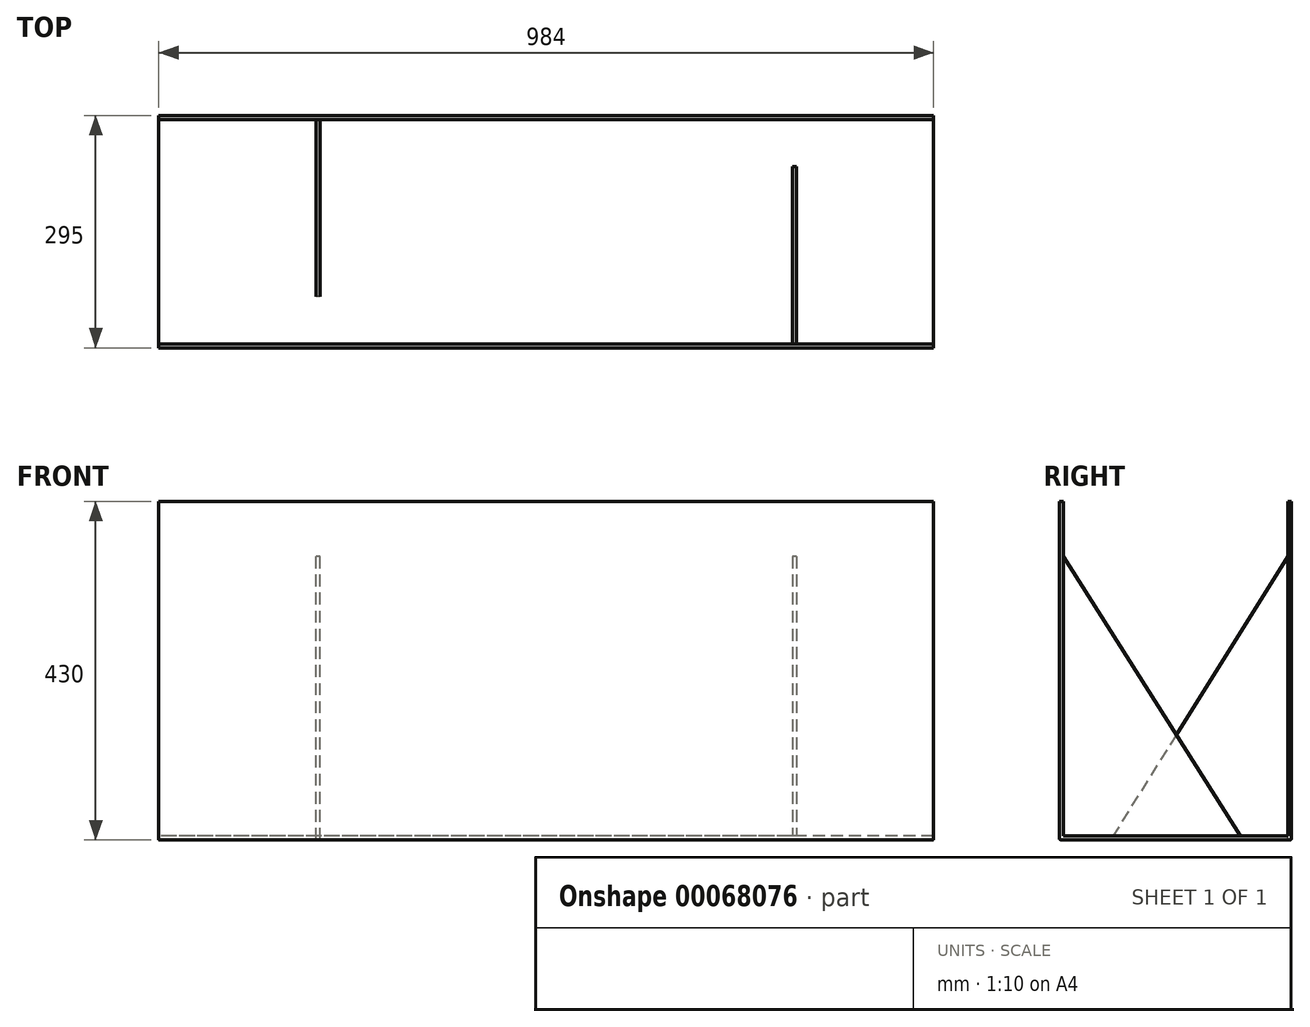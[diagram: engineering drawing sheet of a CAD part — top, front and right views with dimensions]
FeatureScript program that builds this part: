
annotation { "Feature Type Name" : "Feature", "Feature Type Description" : "" }
export const myFeature = defineFeature(function(context is Context, id is Id, definition is map)
    precondition{}
    {
        {
            var Q0;
            Q0=qCreatedBy(makeId("Right.planeOp"),FACE);
            var sketch = newSketch(context, id + "F0", { "sketchPlane" : qUnion([Q0])});
            skLineSegment(sketch, "E0.left", {"start": v(0, 0) * mm, "end": v(0, 430) * mm});
            skLineSegment(sketch, "E1", {"start": v(0, 0) * mm, "end": v(-295, 0) * mm});
            skLineSegment(sketch, "E2", {"start": v(-295, 0) * mm, "end": v(-295, 430) * mm});
            skLineSegment(sketch, "E3.0", {"start": v(-290, 5) * mm, "end": v(-290, 430) * mm});
            skLineSegment(sketch, "E3.1", {"start": v(-5, 5) * mm, "end": v(-290, 5) * mm});
            skLineSegment(sketch, "E3.2", {"start": v(-5, 5) * mm, "end": v(-5, 430) * mm});
            skLineSegment(sketch, "E4", {"start": v(0, 430) * mm, "end": v(-5, 430) * mm});
            skLineSegment(sketch, "E5", {"start": v(-290, 430) * mm, "end": v(-295, 430) * mm});
            skSolve(sketch);
        }
        {
            var Q0;
            Q0=makeQuery(id+"F0.imprint","IMPRINT",FACE,{"disambiguationData":[TD([[makeQuery(id+"F0.imprint","IMPRINT",EDGE,{"derivedFrom":sQuery(id+"F0.wireOp",EDGE,"E0.bottom")}),-1.0]])]});
            var Q1;
            Q1=makeQuery(id+"F0.imprint","IMPRINT",FACE,{"disambiguationData":[TD([[makeQuery(id+"F0.imprint","IMPRINT",EDGE,{"derivedFrom":sQuery(id+"F0.wireOp",EDGE,"E0.left")}),1.0]])]});
            extrude(context, id + "F1", {"entities" : qUnion([Q0, Q1]), "depth" : 984 * mm});
        }
        {
            var Q0;
            Q0=qCreatedBy(makeId("Right.planeOp"),FACE);
            cPlane(context, id + "F2", {"entities" : qUnion([Q0]), "cplaneType" : CPlaneType.OFFSET, "offset" : 200 * mm, "width" : 150 * mm, "height" : 150 * mm});
        }
        {
            var Q0;
            Q0=qCreatedBy(id+"F2.planeOp",FACE);
            var sketch = newSketch(context, id + "F3", { "sketchPlane" : qUnion([Q0])});
            skLineSegment(sketch, "E6.0", {"start": v(-5, 0) * mm, "end": v(-5, 360) * mm});
            skLineSegment(sketch, "E7.0", {"start": v(-5, 0) * mm, "end": v(-230, 0) * mm});
            skPoint(sketch, "E8", {"position": v(-230, 0) * mm});
            skPoint(sketch, "E9", {"position": v(-5, 360) * mm});
            skLineSegment(sketch, "E10", {"start": v(-5, 360) * mm, "end": v(-230, 0) * mm});
            skSolve(sketch);
        }
        {
            var Q0;
            Q0=makeQuery(id+"F3.imprint","IMPRINT",FACE,{"disambiguationData":[TD([[makeQuery(id+"F3.imprint","IMPRINT",EDGE,{"derivedFrom":sQuery(id+"F3.wireOp",EDGE,"E6.0")}),1.0]])]});
            extrude(context, id + "F4", {"entities" : qUnion([Q0]), "depth" : 5 * mm});
        }
        {
            var Q0;
            Q0=makeQuery(id+"F4.opExtrude","CAP_FACE",FACE,{"disambiguationData":[OSD([sQuery(id+"F3.wireOp",EDGE,"E6.0"),sQuery(id+"F3.wireOp",EDGE,"E7.0"),sQuery(id+"F3.wireOp",EDGE,"E10")])],"isStart":false});
            cPlane(context, id + "F5", {"entities" : qUnion([Q0]), "cplaneType" : CPlaneType.OFFSET, "offset" : 600 * mm, "width" : 150 * mm, "height" : 150 * mm});
        }
        {
            var Q0;
            Q0=qCreatedBy(id+"F5.planeOp",FACE);
            var sketch = newSketch(context, id + "F6", { "sketchPlane" : qUnion([Q0])});
            skLineSegment(sketch, "E11", {"start": v(-290, 5) * mm, "end": v(-65, 5) * mm});
            skLineSegment(sketch, "E12", {"start": v(-65, 5) * mm, "end": v(-290, 360) * mm});
            skLineSegment(sketch, "E13", {"start": v(-290, 360) * mm, "end": v(-290, 5) * mm});
            skSolve(sketch);
        }
        {
            var Q0;
            Q0=makeQuery(id+"F6.imprint","IMPRINT",FACE,{"disambiguationData":[TD([[makeQuery(id+"F6.imprint","IMPRINT",EDGE,{"derivedFrom":sQuery(id+"F6.wireOp",EDGE,"E11")}),1.0]])]});
            extrude(context, id + "F7", {"entities" : qUnion([Q0]), "operationType" : NewBodyOperationType.ADD, "depth" : 5 * mm});
        }
        {
            var Q0;
            Q0=makeQuery(id+"F1.opExtrude","SWEPT_EDGE",EDGE,{"disambiguationData":[OSD([sQuery(id+"F0.wireOp",EDGE,"E0.left"),sQuery(id+"F0.wireOp",EDGE,"E1")])]});
            var Q1;
            Q1=makeQuery(id+"F1.opExtrude","SWEPT_EDGE",EDGE,{"disambiguationData":[OSD([sQuery(id+"F0.wireOp",EDGE,"E1"),sQuery(id+"F0.wireOp",EDGE,"E2")])]});
            fillet(context, id + "F8", {"entities" : qUnion([Q0, Q1]), "radius" : 2 * mm, "tangentPropagation" : true, "allowEdgeOverflow" : false});
        }
    });
